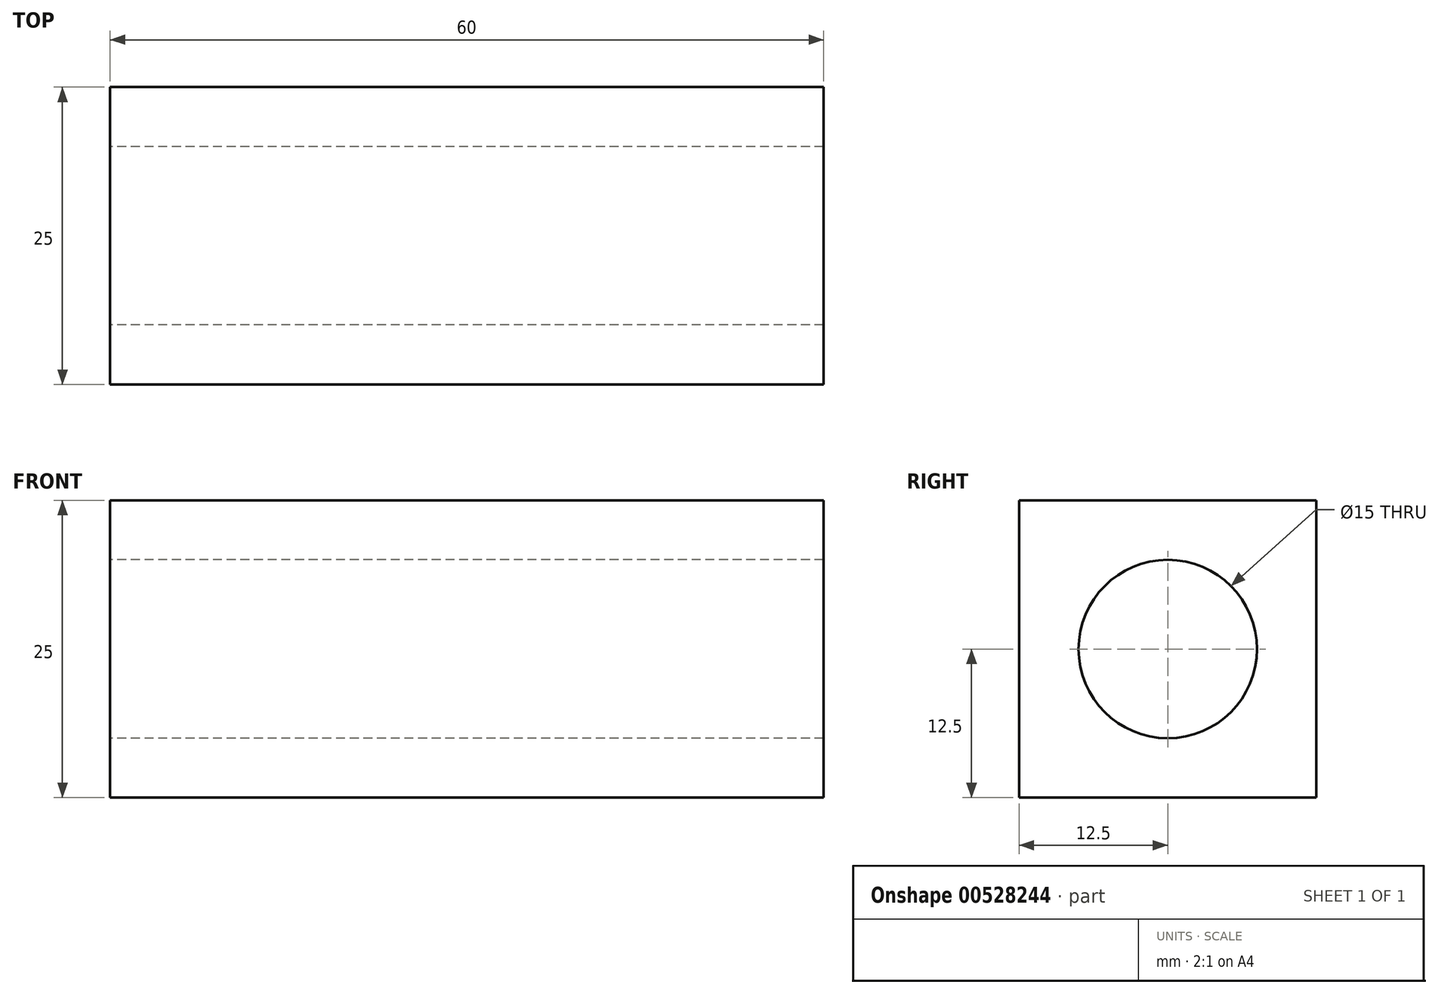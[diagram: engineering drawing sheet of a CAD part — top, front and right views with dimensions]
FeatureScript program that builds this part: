
annotation { "Feature Type Name" : "Feature", "Feature Type Description" : "" }
export const myFeature = defineFeature(function(context is Context, id is Id, definition is map)
    precondition{}
    {
        {
            var Q0;
            Q0=qCreatedBy(makeId("Right.planeOp"),FACE);
            var sketch = newSketch(context, id + "F0", { "sketchPlane" : qUnion([Q0])});
            skLineSegment(sketch, "E0", {"start": v(0, 0) * mm, "end": v(0, 12.5) * mm});
            skLineSegment(sketch, "E1", {"start": v(0, 0) * mm, "end": v(0, -12.5) * mm});
            skLineSegment(sketch, "E2.bottom", {"start": v(0, 12.5) * mm, "end": v(25, 12.5) * mm});
            skLineSegment(sketch, "E2.top", {"start": v(0, -12.5) * mm, "end": v(25, -12.5) * mm});
            skLineSegment(sketch, "E2.left", {"start": v(0, 12.5) * mm, "end": v(0, -12.5) * mm});
            skLineSegment(sketch, "E2.right", {"start": v(25, 12.5) * mm, "end": v(25, -12.5) * mm});
            skCircle(sketch, "E3", {"center": v(12.5, 0) * mm, "radius": 7.5 * mm});
            skPoint(sketch, "E3.centerSnap0", {"position": v(12.5, -12.5) * mm});
            skSolve(sketch);
        }
        {
            var Q0;
            Q0=makeQuery(id+"F0.imprint","IMPRINT",FACE,{"disambiguationData":[TD([[makeQuery(id+"F0.imprint","IMPRINT",EDGE,{"derivedFrom":sQuery(id+"F0.wireOp",EDGE,"E2.bottom")}),-1.0]])]});
            extrude(context, id + "F1", {"entities" : qUnion([Q0]), "depth" : 60 * mm, "offsetDistance" : 25 * mm});
        }
    });
